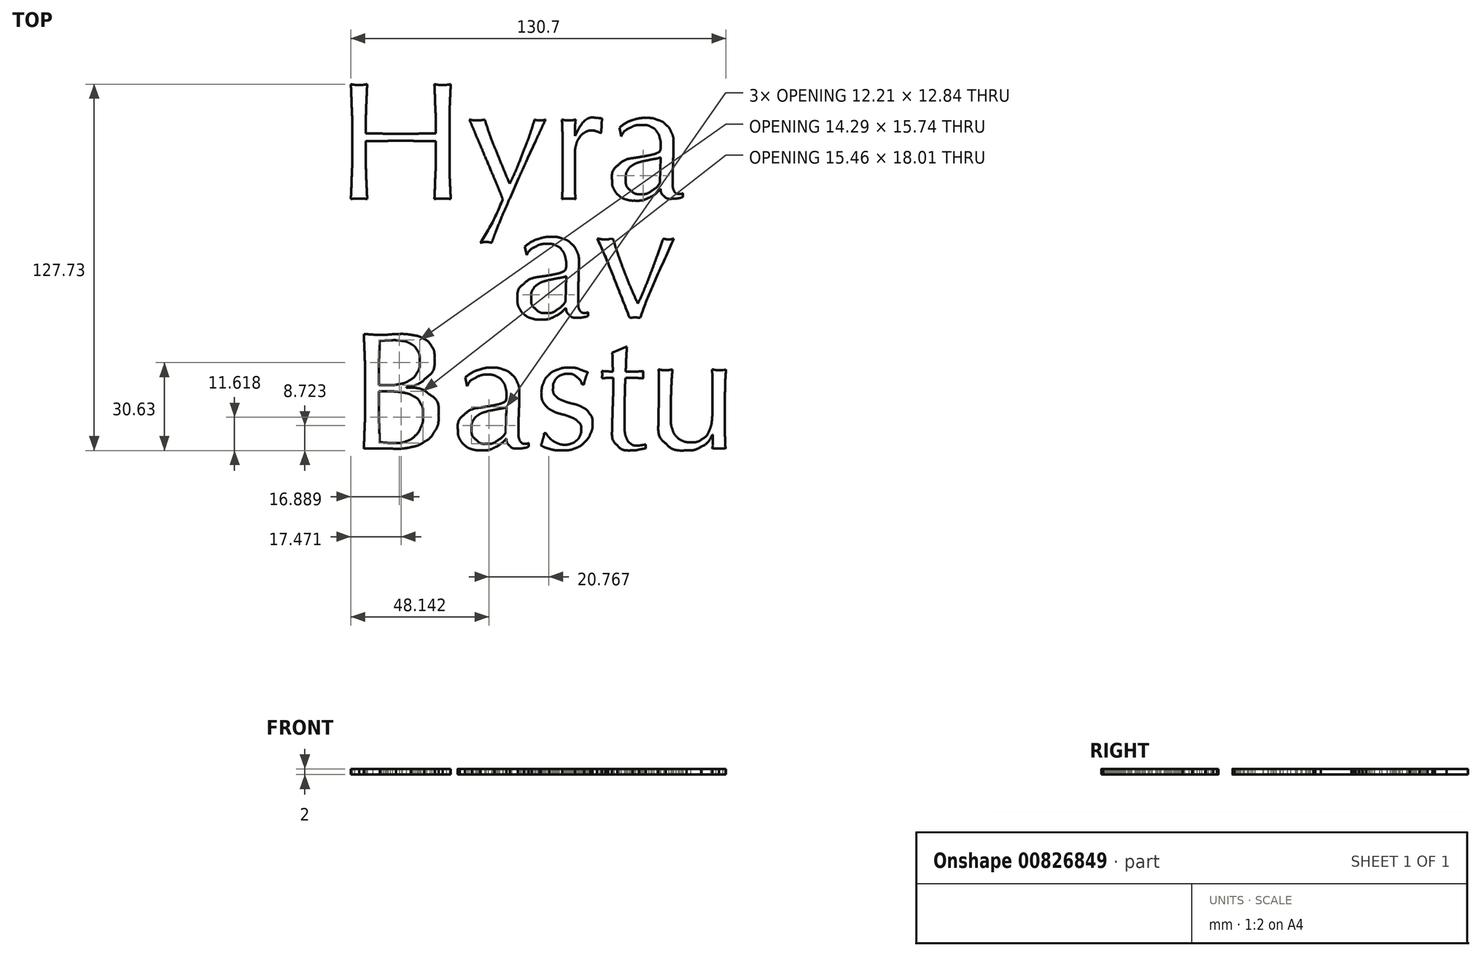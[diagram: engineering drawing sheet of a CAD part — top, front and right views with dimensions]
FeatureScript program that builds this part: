
annotation { "Feature Type Name" : "Feature", "Feature Type Description" : "" }
export const myFeature = defineFeature(function(context is Context, id is Id, definition is map)
    precondition{}
    {
        {
            var Q0;
            Q0=qCreatedBy(makeId("Top.planeOp"),FACE);
            var sketch = newSketch(context, id + "F0", { "sketchPlane" : qUnion([Q0])});
            skFitSpline(sketch, "E0", {"points": [v(-37.85, 47.17) * mm, v(-39.94, 47.13) * mm, v(-41.98, 47.09) * mm, v(-43.96, 47.05) * mm]});
            skFitSpline(sketch, "E1", {"points": [v(-43.96, 47.05) * mm, v(-45.9, 47.01) * mm, v(-47.92, 47) * mm, v(-50.01, 47) * mm]});
            skFitSpline(sketch, "E2", {"points": [v(-50.01, 47) * mm, v(-52.11, 47) * mm, v(-54.15, 47.01) * mm, v(-56.13, 47.05) * mm]});
            skFitSpline(sketch, "E3", {"points": [v(-56.13, 47.05) * mm, v(-58.07, 47.09) * mm, v(-60.09, 47.13) * mm, v(-62.18, 47.17) * mm]});
            skLineSegment(sketch, "E4", {"start": v(-37.85, 49.2) * mm, "end": v(-37.85, 47.17) * mm});
            skLineSegment(sketch, "E5", {"start": v(-37.85, 47.17) * mm, "end": v(-37.85, 49.2) * mm});
            skFitSpline(sketch, "E6", {"points": [v(-62.18, 49.2) * mm, v(-62.18, 51.77) * mm, v(-62.14, 54.27) * mm, v(-62.07, 56.72) * mm]});
            skFitSpline(sketch, "E7", {"points": [v(-62.07, 56.72) * mm, v(-61.95, 59.2) * mm, v(-61.83, 61.72) * mm, v(-61.72, 64.29) * mm]});
            skFitSpline(sketch, "E8", {"points": [v(-61.72, 64.29) * mm, v(-62.22, 64.2) * mm, v(-62.7, 64.13) * mm, v(-63.17, 64.05) * mm]});
            skFitSpline(sketch, "E9", {"points": [v(-63.17, 64.05) * mm, v(-63.64, 64.01) * mm, v(-64.1, 64) * mm, v(-64.57, 64) * mm]});
            skFitSpline(sketch, "E10", {"points": [v(-64.57, 64) * mm, v(-65.04, 64) * mm, v(-65.5, 64.01) * mm, v(-65.97, 64.05) * mm]});
            skFitSpline(sketch, "E11", {"points": [v(-65.97, 64.05) * mm, v(-66.43, 64.13) * mm, v(-66.92, 64.2) * mm, v(-67.42, 64.29) * mm]});
            skFitSpline(sketch, "E12", {"points": [v(-67.42, 64.29) * mm, v(-67.3, 61.72) * mm, v(-67.2, 59.2) * mm, v(-67.13, 56.72) * mm]});
            skFitSpline(sketch, "E13", {"points": [v(-67.13, 56.72) * mm, v(-67.02, 54.27) * mm, v(-66.96, 51.77) * mm, v(-66.96, 49.2) * mm]});
            skLineSegment(sketch, "E14", {"start": v(-62.18, 47.17) * mm, "end": v(-62.18, 49.2) * mm});
            skLineSegment(sketch, "E15", {"start": v(-62.18, 49.2) * mm, "end": v(-62.18, 47.17) * mm});
            skFitSpline(sketch, "E16", {"points": [v(-66.96, 39.2) * mm, v(-66.96, 36.63) * mm, v(-67.02, 34.1) * mm, v(-67.13, 31.62) * mm]});
            skFitSpline(sketch, "E17", {"points": [v(-67.13, 31.62) * mm, v(-67.2, 29.14) * mm, v(-67.3, 26.7) * mm, v(-67.42, 24.29) * mm]});
            skFitSpline(sketch, "E18", {"points": [v(-67.42, 24.29) * mm, v(-66.53, 24.36) * mm, v(-65.58, 24.4) * mm, v(-64.57, 24.4) * mm]});
            skFitSpline(sketch, "E19", {"points": [v(-64.57, 24.4) * mm, v(-63.56, 24.4) * mm, v(-62.61, 24.36) * mm, v(-61.72, 24.29) * mm]});
            skFitSpline(sketch, "E20", {"points": [v(-61.72, 24.29) * mm, v(-61.83, 26.7) * mm, v(-61.95, 29.14) * mm, v(-62.07, 31.62) * mm]});
            skFitSpline(sketch, "E21", {"points": [v(-62.07, 31.62) * mm, v(-62.14, 34.1) * mm, v(-62.18, 36.63) * mm, v(-62.18, 39.2) * mm]});
            skLineSegment(sketch, "E22", {"start": v(-66.96, 49.2) * mm, "end": v(-66.96, 39.2) * mm});
            skLineSegment(sketch, "E23", {"start": v(-66.96, 39.2) * mm, "end": v(-66.96, 49.2) * mm});
            skFitSpline(sketch, "E24", {"points": [v(-62.18, 44.43) * mm, v(-60.09, 44.47) * mm, v(-58.07, 44.49) * mm, v(-56.13, 44.49) * mm]});
            skFitSpline(sketch, "E25", {"points": [v(-56.13, 44.49) * mm, v(-54.15, 44.53) * mm, v(-52.11, 44.55) * mm, v(-50.01, 44.55) * mm]});
            skFitSpline(sketch, "E26", {"points": [v(-50.01, 44.55) * mm, v(-47.92, 44.55) * mm, v(-45.9, 44.53) * mm, v(-43.96, 44.49) * mm]});
            skFitSpline(sketch, "E27", {"points": [v(-43.96, 44.49) * mm, v(-41.98, 44.49) * mm, v(-39.94, 44.47) * mm, v(-37.85, 44.43) * mm]});
            skLineSegment(sketch, "E28", {"start": v(-62.18, 39.2) * mm, "end": v(-62.18, 44.43) * mm});
            skLineSegment(sketch, "E29", {"start": v(-62.18, 44.43) * mm, "end": v(-62.18, 39.2) * mm});
            skFitSpline(sketch, "E30", {"points": [v(-37.85, 39.2) * mm, v(-37.85, 36.63) * mm, v(-37.9, 34.1) * mm, v(-38.02, 31.62) * mm]});
            skFitSpline(sketch, "E31", {"points": [v(-38.02, 31.62) * mm, v(-38.1, 29.14) * mm, v(-38.2, 26.7) * mm, v(-38.31, 24.29) * mm]});
            skFitSpline(sketch, "E32", {"points": [v(-38.31, 24.29) * mm, v(-37.42, 24.36) * mm, v(-36.47, 24.4) * mm, v(-35.46, 24.4) * mm]});
            skFitSpline(sketch, "E33", {"points": [v(-35.46, 24.4) * mm, v(-34.45, 24.4) * mm, v(-33.5, 24.36) * mm, v(-32.6, 24.29) * mm]});
            skFitSpline(sketch, "E34", {"points": [v(-32.6, 24.29) * mm, v(-32.72, 26.7) * mm, v(-32.84, 29.14) * mm, v(-32.95, 31.62) * mm]});
            skFitSpline(sketch, "E35", {"points": [v(-32.95, 31.62) * mm, v(-33.03, 34.1) * mm, v(-33.07, 36.63) * mm, v(-33.07, 39.2) * mm]});
            skLineSegment(sketch, "E36", {"start": v(-37.85, 44.43) * mm, "end": v(-37.85, 39.2) * mm});
            skLineSegment(sketch, "E37", {"start": v(-37.85, 39.2) * mm, "end": v(-37.85, 44.43) * mm});
            skFitSpline(sketch, "E38", {"points": [v(-33.07, 49.2) * mm, v(-33.07, 51.77) * mm, v(-33.03, 54.27) * mm, v(-32.95, 56.72) * mm]});
            skFitSpline(sketch, "E39", {"points": [v(-32.95, 56.72) * mm, v(-32.84, 59.2) * mm, v(-32.72, 61.72) * mm, v(-32.6, 64.29) * mm]});
            skFitSpline(sketch, "E40", {"points": [v(-32.6, 64.29) * mm, v(-33.1, 64.2) * mm, v(-33.6, 64.13) * mm, v(-34.06, 64.05) * mm]});
            skFitSpline(sketch, "E41", {"points": [v(-34.06, 64.05) * mm, v(-34.53, 64.01) * mm, v(-35, 64) * mm, v(-35.46, 64) * mm]});
            skFitSpline(sketch, "E42", {"points": [v(-35.46, 64) * mm, v(-35.92, 64) * mm, v(-36.39, 64.01) * mm, v(-36.86, 64.05) * mm]});
            skFitSpline(sketch, "E43", {"points": [v(-36.86, 64.05) * mm, v(-37.32, 64.13) * mm, v(-37.8, 64.2) * mm, v(-38.31, 64.29) * mm]});
            skFitSpline(sketch, "E44", {"points": [v(-38.31, 64.29) * mm, v(-38.2, 61.72) * mm, v(-38.1, 59.2) * mm, v(-38.02, 56.72) * mm]});
            skFitSpline(sketch, "E45", {"points": [v(-38.02, 56.72) * mm, v(-37.9, 54.27) * mm, v(-37.85, 51.77) * mm, v(-37.85, 49.2) * mm]});
            skLineSegment(sketch, "E46", {"start": v(-33.07, 39.2) * mm, "end": v(-33.07, 49.2) * mm});
            skLineSegment(sketch, "E47", {"start": v(-33.07, 49.2) * mm, "end": v(-33.07, 39.2) * mm});
            skFitSpline(sketch, "E48", {"points": [v(-14.48, 24.23) * mm, v(-16.61, 19.14) * mm, v(-19.21, 14.06) * mm, v(-22.28, 8.97) * mm]});
            skFitSpline(sketch, "E49", {"points": [v(-22.28, 8.97) * mm, v(-21.5, 9.17) * mm, v(-20.84, 9.26) * mm, v(-20.3, 9.26) * mm]});
            skFitSpline(sketch, "E50", {"points": [v(-20.3, 9.26) * mm, v(-19.76, 9.26) * mm, v(-19.1, 9.17) * mm, v(-18.32, 8.97) * mm]});
            skFitSpline(sketch, "E51", {"points": [v(-18.32, 8.97) * mm, v(-18, 9.94) * mm, v(-17.54, 11.26) * mm, v(-16.92, 12.93) * mm]});
            skFitSpline(sketch, "E52", {"points": [v(-16.92, 12.93) * mm, v(-16.26, 14.56) * mm, v(-15.5, 16.4) * mm, v(-14.65, 18.46) * mm]});
            skFitSpline(sketch, "E53", {"points": [v(-14.65, 18.46) * mm, v(-13.8, 20.48) * mm, v(-12.87, 22.62) * mm, v(-11.86, 24.87) * mm]});
            skFitSpline(sketch, "E54", {"points": [v(-11.86, 24.87) * mm, v(-10.85, 27.16) * mm, v(-9.84, 29.45) * mm, v(-8.83, 31.74) * mm]});
            skFitSpline(sketch, "E55", {"points": [v(-8.83, 31.74) * mm, v(-7.78, 34.07) * mm, v(-6.77, 36.32) * mm, v(-5.8, 38.5) * mm]});
            skFitSpline(sketch, "E56", {"points": [v(-5.8, 38.5) * mm, v(-4.8, 40.7) * mm, v(-3.88, 42.7) * mm, v(-3.07, 44.49) * mm]});
            skFitSpline(sketch, "E57", {"points": [v(-3.07, 44.49) * mm, v(-2.21, 46.31) * mm, v(-1.5, 47.87) * mm, v(-0.91, 49.15) * mm]});
            skFitSpline(sketch, "E58", {"points": [v(-0.91, 49.15) * mm, v(-0.3, 50.47) * mm, v(0.16, 51.4) * mm, v(0.43, 51.94) * mm]});
            skFitSpline(sketch, "E59", {"points": [v(0.43, 51.94) * mm, v(-0.35, 51.75) * mm, v(-0.99, 51.65) * mm, v(-1.5, 51.65) * mm]});
            skFitSpline(sketch, "E60", {"points": [v(-1.5, 51.65) * mm, v(-2, 51.65) * mm, v(-2.64, 51.75) * mm, v(-3.42, 51.94) * mm]});
            skFitSpline(sketch, "E61", {"points": [v(-3.42, 51.94) * mm, v(-4.58, 48.22) * mm, v(-5.92, 44.41) * mm, v(-7.43, 40.53) * mm]});
            skFitSpline(sketch, "E62", {"points": [v(-7.43, 40.53) * mm, v(-8.9, 36.65) * mm, v(-10.46, 33) * mm, v(-12.1, 29.58) * mm]});
            skFitSpline(sketch, "E63", {"points": [v(-12.1, 29.58) * mm, v(-13.72, 33.47) * mm, v(-15.27, 37.23) * mm, v(-16.75, 40.88) * mm]});
            skFitSpline(sketch, "E64", {"points": [v(-16.75, 40.88) * mm, v(-18.22, 44.53) * mm, v(-19.56, 48.22) * mm, v(-20.77, 51.94) * mm]});
            skFitSpline(sketch, "E65", {"points": [v(-20.77, 51.94) * mm, v(-21.27, 51.86) * mm, v(-21.74, 51.79) * mm, v(-22.16, 51.7) * mm]});
            skFitSpline(sketch, "E66", {"points": [v(-22.16, 51.7) * mm, v(-22.6, 51.67) * mm, v(-23.02, 51.65) * mm, v(-23.44, 51.65) * mm]});
            skFitSpline(sketch, "E67", {"points": [v(-23.44, 51.65) * mm, v(-23.87, 51.65) * mm, v(-24.3, 51.67) * mm, v(-24.73, 51.7) * mm]});
            skFitSpline(sketch, "E68", {"points": [v(-24.73, 51.7) * mm, v(-25.15, 51.79) * mm, v(-25.62, 51.86) * mm, v(-26.12, 51.94) * mm]});
            skFitSpline(sketch, "E69", {"points": [v(-26.12, 51.94) * mm, v(-25.85, 51.32) * mm, v(-25.44, 50.37) * mm, v(-24.9, 49.09) * mm]});
            skFitSpline(sketch, "E70", {"points": [v(-24.9, 49.09) * mm, v(-24.36, 47.8) * mm, v(-23.74, 46.31) * mm, v(-23.04, 44.6) * mm]});
            skFitSpline(sketch, "E71", {"points": [v(-23.04, 44.6) * mm, v(-22.3, 42.94) * mm, v(-21.52, 41.13) * mm, v(-20.7, 39.2) * mm]});
            skFitSpline(sketch, "E72", {"points": [v(-20.7, 39.2) * mm, v(-19.9, 37.29) * mm, v(-19.1, 35.4) * mm, v(-18.32, 33.54) * mm]});
            skFitSpline(sketch, "E73", {"points": [v(-18.32, 33.54) * mm, v(-17.54, 31.72) * mm, v(-16.83, 29.97) * mm, v(-16.17, 28.3) * mm]});
            skFitSpline(sketch, "E74", {"points": [v(-16.17, 28.3) * mm, v(-15.47, 26.63) * mm, v(-14.9, 25.28) * mm, v(-14.48, 24.23) * mm]});
            skFitSpline(sketch, "E75", {"points": [v(19.87, 47.46) * mm, v(19.87, 48.23) * mm, v(19.9, 49.09) * mm, v(19.93, 50.02) * mm]});
            skFitSpline(sketch, "E76", {"points": [v(19.93, 50.02) * mm, v(19.97, 51) * mm, v(20.09, 51.7) * mm, v(20.28, 52.17) * mm]});
            skFitSpline(sketch, "E77", {"points": [v(20.28, 52.17) * mm, v(19.9, 52.33) * mm, v(19.56, 52.43) * mm, v(19.3, 52.47) * mm]});
            skFitSpline(sketch, "E78", {"points": [v(19.3, 52.47) * mm, v(19.06, 52.5) * mm, v(18.77, 52.52) * mm, v(18.42, 52.52) * mm]});
            skFitSpline(sketch, "E79", {"points": [v(18.42, 52.52) * mm, v(15.59, 52.52) * mm, v(13.02, 50.43) * mm, v(10.73, 46.24) * mm]});
            skLineSegment(sketch, "E80", {"start": v(19.47, 47.17) * mm, "end": v(19.87, 47.46) * mm});
            skLineSegment(sketch, "E81", {"start": v(19.87, 47.46) * mm, "end": v(19.47, 47.17) * mm});
            skFitSpline(sketch, "E82", {"points": [v(10.62, 46.3) * mm, v(10.62, 47.03) * mm, v(10.62, 47.8) * mm, v(10.62, 48.62) * mm]});
            skFitSpline(sketch, "E83", {"points": [v(10.62, 48.62) * mm, v(10.66, 49.44) * mm, v(10.75, 50.54) * mm, v(10.9, 51.94) * mm]});
            skFitSpline(sketch, "E84", {"points": [v(10.9, 51.94) * mm, v(10.48, 51.86) * mm, v(10.07, 51.79) * mm, v(9.69, 51.7) * mm]});
            skFitSpline(sketch, "E85", {"points": [v(9.69, 51.7) * mm, v(9.3, 51.67) * mm, v(8.93, 51.65) * mm, v(8.58, 51.65) * mm]});
            skFitSpline(sketch, "E86", {"points": [v(8.58, 51.65) * mm, v(8.15, 51.65) * mm, v(7.74, 51.67) * mm, v(7.36, 51.7) * mm]});
            skFitSpline(sketch, "E87", {"points": [v(7.36, 51.7) * mm, v(6.97, 51.79) * mm, v(6.56, 51.86) * mm, v(6.13, 51.94) * mm]});
            skFitSpline(sketch, "E88", {"points": [v(6.13, 51.94) * mm, v(6.25, 49.38) * mm, v(6.3, 47.1) * mm, v(6.3, 45.13) * mm]});
            skFitSpline(sketch, "E89", {"points": [v(6.3, 45.13) * mm, v(6.35, 43.15) * mm, v(6.37, 41.4) * mm, v(6.37, 39.89) * mm]});
            skLineSegment(sketch, "E90", {"start": v(10.73, 46.24) * mm, "end": v(10.62, 46.3) * mm});
            skLineSegment(sketch, "E91", {"start": v(10.62, 46.3) * mm, "end": v(10.73, 46.24) * mm});
            skFitSpline(sketch, "E92", {"points": [v(6.37, 38.03) * mm, v(6.37, 34.73) * mm, v(6.35, 31.93) * mm, v(6.3, 29.64) * mm]});
            skFitSpline(sketch, "E93", {"points": [v(6.3, 29.64) * mm, v(6.3, 27.4) * mm, v(6.25, 25.6) * mm, v(6.13, 24.29) * mm]});
            skFitSpline(sketch, "E94", {"points": [v(6.13, 24.29) * mm, v(6.91, 24.36) * mm, v(7.73, 24.4) * mm, v(8.58, 24.4) * mm]});
            skFitSpline(sketch, "E95", {"points": [v(8.58, 24.4) * mm, v(9.36, 24.4) * mm, v(10.13, 24.36) * mm, v(10.9, 24.29) * mm]});
            skFitSpline(sketch, "E96", {"points": [v(10.9, 24.29) * mm, v(10.8, 25.14) * mm, v(10.71, 26.25) * mm, v(10.68, 27.6) * mm]});
            skFitSpline(sketch, "E97", {"points": [v(10.68, 27.6) * mm, v(10.68, 29) * mm, v(10.68, 31) * mm, v(10.68, 33.6) * mm]});
            skLineSegment(sketch, "E98", {"start": v(6.37, 39.89) * mm, "end": v(6.37, 38.03) * mm});
            skLineSegment(sketch, "E99", {"start": v(6.37, 38.03) * mm, "end": v(6.37, 39.89) * mm});
            skFitSpline(sketch, "E100", {"points": [v(10.68, 40) * mm, v(10.68, 41.13) * mm, v(10.81, 42.18) * mm, v(11.08, 43.15) * mm]});
            skFitSpline(sketch, "E101", {"points": [v(11.08, 43.15) * mm, v(11.35, 44.16) * mm, v(11.74, 45.01) * mm, v(12.25, 45.71) * mm]});
            skFitSpline(sketch, "E102", {"points": [v(12.25, 45.71) * mm, v(12.75, 46.45) * mm, v(13.37, 47.03) * mm, v(14.11, 47.46) * mm]});
            skFitSpline(sketch, "E103", {"points": [v(14.11, 47.46) * mm, v(14.85, 47.89) * mm, v(15.68, 48.1) * mm, v(16.61, 48.1) * mm]});
            skFitSpline(sketch, "E104", {"points": [v(16.61, 48.1) * mm, v(17.2, 48.1) * mm, v(17.76, 48) * mm, v(18.3, 47.8) * mm]});
            skFitSpline(sketch, "E105", {"points": [v(18.3, 47.8) * mm, v(18.88, 47.61) * mm, v(19.27, 47.4) * mm, v(19.47, 47.17) * mm]});
            skLineSegment(sketch, "E106", {"start": v(10.68, 33.6) * mm, "end": v(10.68, 40) * mm});
            skLineSegment(sketch, "E107", {"start": v(10.68, 40) * mm, "end": v(10.68, 33.6) * mm});
            skFitSpline(sketch, "E108", {"points": [v(40.31, 30.05) * mm, v(39.65, 28.96) * mm, v(38.7, 28.01) * mm, v(37.46, 27.2) * mm]});
            skFitSpline(sketch, "E109", {"points": [v(37.46, 27.2) * mm, v(36.25, 26.38) * mm, v(34.91, 25.97) * mm, v(33.44, 25.97) * mm]});
            skFitSpline(sketch, "E110", {"points": [v(33.44, 25.97) * mm, v(32.16, 25.97) * mm, v(31, 26.44) * mm, v(29.95, 27.37) * mm]});
            skFitSpline(sketch, "E111", {"points": [v(29.95, 27.37) * mm, v(28.9, 28.3) * mm, v(28.37, 29.68) * mm, v(28.37, 31.5) * mm]});
            skFitSpline(sketch, "E112", {"points": [v(28.37, 31.5) * mm, v(28.37, 32.6) * mm, v(28.57, 33.48) * mm, v(28.96, 34.18) * mm]});
            skFitSpline(sketch, "E113", {"points": [v(28.96, 34.18) * mm, v(29.38, 34.88) * mm, v(29.93, 35.46) * mm, v(30.59, 35.93) * mm]});
            skFitSpline(sketch, "E114", {"points": [v(30.59, 35.93) * mm, v(31.29, 36.4) * mm, v(32.06, 36.76) * mm, v(32.92, 37.04) * mm]});
            skFitSpline(sketch, "E115", {"points": [v(32.92, 37.04) * mm, v(33.8, 37.3) * mm, v(34.7, 37.52) * mm, v(35.6, 37.68) * mm]});
            skFitSpline(sketch, "E116", {"points": [v(35.6, 37.68) * mm, v(36.49, 37.87) * mm, v(37.36, 38.05) * mm, v(38.21, 38.2) * mm]});
            skFitSpline(sketch, "E117", {"points": [v(38.21, 38.2) * mm, v(39.1, 38.36) * mm, v(39.88, 38.55) * mm, v(40.54, 38.78) * mm]});
            skLineSegment(sketch, "E118", {"start": v(40.54, 38.78) * mm, "end": v(40.31, 30.05) * mm});
            skLineSegment(sketch, "E119", {"start": v(40.31, 30.05) * mm, "end": v(40.54, 38.78) * mm});
            skFitSpline(sketch, "E120", {"points": [v(26.8, 46.12) * mm, v(27.46, 47.36) * mm, v(28.45, 48.33) * mm, v(29.77, 49.03) * mm]});
            skFitSpline(sketch, "E121", {"points": [v(29.77, 49.03) * mm, v(31.13, 49.73) * mm, v(32.59, 50.08) * mm, v(34.14, 50.08) * mm]});
            skFitSpline(sketch, "E122", {"points": [v(34.14, 50.08) * mm, v(35.3, 50.08) * mm, v(36.3, 49.87) * mm, v(37.1, 49.44) * mm]});
            skFitSpline(sketch, "E123", {"points": [v(37.1, 49.44) * mm, v(37.92, 49.05) * mm, v(38.58, 48.53) * mm, v(39.09, 47.87) * mm]});
            skFitSpline(sketch, "E124", {"points": [v(39.09, 47.87) * mm, v(39.6, 47.2) * mm, v(39.96, 46.43) * mm, v(40.2, 45.54) * mm]});
            skFitSpline(sketch, "E125", {"points": [v(40.2, 45.54) * mm, v(40.43, 44.64) * mm, v(40.54, 43.71) * mm, v(40.54, 42.74) * mm]});
            skFitSpline(sketch, "E126", {"points": [v(40.54, 42.74) * mm, v(40.54, 42.16) * mm, v(40.49, 41.67) * mm, v(40.37, 41.29) * mm]});
            skFitSpline(sketch, "E127", {"points": [v(40.37, 41.29) * mm, v(40.25, 40.94) * mm, v(39.9, 40.63) * mm, v(39.32, 40.36) * mm]});
            skFitSpline(sketch, "E128", {"points": [v(39.32, 40.36) * mm, v(38.78, 40.08) * mm, v(37.9, 39.81) * mm, v(36.7, 39.54) * mm]});
            skFitSpline(sketch, "E129", {"points": [v(36.7, 39.54) * mm, v(35.54, 39.3) * mm, v(33.9, 39.02) * mm, v(31.8, 38.67) * mm]});
            skFitSpline(sketch, "E130", {"points": [v(31.8, 38.67) * mm, v(29.25, 38.24) * mm, v(27.23, 37.39) * mm, v(25.75, 36.1) * mm]});
            skFitSpline(sketch, "E131", {"points": [v(25.75, 36.1) * mm, v(24.32, 34.82) * mm, v(23.6, 33.02) * mm, v(23.6, 30.69) * mm]});
            skFitSpline(sketch, "E132", {"points": [v(23.6, 30.69) * mm, v(23.6, 29.56) * mm, v(23.81, 28.56) * mm, v(24.24, 27.66) * mm]});
            skFitSpline(sketch, "E133", {"points": [v(24.24, 27.66) * mm, v(24.7, 26.8) * mm, v(25.29, 26.07) * mm, v(25.99, 25.45) * mm]});
            skFitSpline(sketch, "E134", {"points": [v(25.99, 25.45) * mm, v(26.72, 24.83) * mm, v(27.56, 24.38) * mm, v(28.5, 24.11) * mm]});
            skFitSpline(sketch, "E135", {"points": [v(28.5, 24.11) * mm, v(29.42, 23.84) * mm, v(30.37, 23.7) * mm, v(31.34, 23.7) * mm]});
            skFitSpline(sketch, "E136", {"points": [v(31.34, 23.7) * mm, v(33.32, 23.7) * mm, v(35, 24.03) * mm, v(36.35, 24.7) * mm]});
            skFitSpline(sketch, "E137", {"points": [v(36.35, 24.7) * mm, v(37.7, 25.35) * mm, v(39.09, 26.38) * mm, v(40.49, 27.78) * mm]});
            skFitSpline(sketch, "E138", {"points": [v(40.49, 27.78) * mm, v(40.6, 26.77) * mm, v(40.99, 25.93) * mm, v(41.65, 25.28) * mm]});
            skFitSpline(sketch, "E139", {"points": [v(41.65, 25.28) * mm, v(42.3, 24.65) * mm, v(43.26, 24.34) * mm, v(44.5, 24.34) * mm]});
            skFitSpline(sketch, "E140", {"points": [v(44.5, 24.34) * mm, v(45.28, 24.34) * mm, v(45.98, 24.4) * mm, v(46.6, 24.52) * mm]});
            skFitSpline(sketch, "E141", {"points": [v(46.6, 24.52) * mm, v(47.26, 24.63) * mm, v(47.8, 24.79) * mm, v(48.23, 24.98) * mm]});
            skLineSegment(sketch, "E142", {"start": v(26.16, 49.15) * mm, "end": v(26.16, 46.12) * mm});
            skLineSegment(sketch, "E143", {"start": v(26.16, 46.12) * mm, "end": v(26.8, 46.12) * mm});
            skLineSegment(sketch, "E144", {"start": v(26.8, 46.12) * mm, "end": v(26.16, 49.15) * mm});
            skFitSpline(sketch, "E145", {"points": [v(48.23, 26.26) * mm, v(48.03, 26.15) * mm, v(47.82, 26.07) * mm, v(47.59, 26.03) * mm]});
            skFitSpline(sketch, "E146", {"points": [v(47.59, 26.03) * mm, v(47.4, 26.03) * mm, v(47.2, 26.03) * mm, v(47, 26.03) * mm]});
            skFitSpline(sketch, "E147", {"points": [v(47, 26.03) * mm, v(46.42, 26.03) * mm, v(45.98, 26.17) * mm, v(45.67, 26.44) * mm]});
            skFitSpline(sketch, "E148", {"points": [v(45.67, 26.44) * mm, v(45.4, 26.71) * mm, v(45.18, 27.04) * mm, v(45.03, 27.43) * mm]});
            skFitSpline(sketch, "E149", {"points": [v(45.03, 27.43) * mm, v(44.87, 27.86) * mm, v(44.77, 28.32) * mm, v(44.74, 28.83) * mm]});
            skFitSpline(sketch, "E150", {"points": [v(44.74, 28.83) * mm, v(44.74, 29.37) * mm, v(44.74, 29.87) * mm, v(44.74, 30.34) * mm]});
            skFitSpline(sketch, "E151", {"points": [v(44.74, 30.34) * mm, v(44.74, 32.79) * mm, v(44.77, 35.1) * mm, v(44.85, 37.27) * mm]});
            skFitSpline(sketch, "E152", {"points": [v(44.85, 37.27) * mm, v(44.93, 39.48) * mm, v(44.97, 41.7) * mm, v(44.97, 43.9) * mm]});
            skFitSpline(sketch, "E153", {"points": [v(44.97, 43.9) * mm, v(44.97, 45.19) * mm, v(44.74, 46.35) * mm, v(44.27, 47.4) * mm]});
            skFitSpline(sketch, "E154", {"points": [v(44.27, 47.4) * mm, v(43.8, 48.49) * mm, v(43.16, 49.4) * mm, v(42.35, 50.14) * mm]});
            skFitSpline(sketch, "E155", {"points": [v(42.35, 50.14) * mm, v(41.53, 50.91) * mm, v(40.54, 51.5) * mm, v(39.38, 51.88) * mm]});
            skFitSpline(sketch, "E156", {"points": [v(39.38, 51.88) * mm, v(38.21, 52.31) * mm, v(36.93, 52.52) * mm, v(35.54, 52.52) * mm]});
            skFitSpline(sketch, "E157", {"points": [v(35.54, 52.52) * mm, v(33.98, 52.52) * mm, v(32.47, 52.3) * mm, v(31, 51.83) * mm]});
            skFitSpline(sketch, "E158", {"points": [v(31, 51.83) * mm, v(29.52, 51.36) * mm, v(27.9, 50.47) * mm, v(26.16, 49.15) * mm]});
            skLineSegment(sketch, "E159", {"start": v(48.23, 24.98) * mm, "end": v(48.23, 26.26) * mm});
            skLineSegment(sketch, "E160", {"start": v(48.23, 26.26) * mm, "end": v(48.23, 24.98) * mm});
            skFitSpline(sketch, "E161", {"points": [v(7.36, -11.42) * mm, v(6.7, -12.5) * mm, v(5.75, -13.45) * mm, v(4.5, -14.27) * mm]});
            skFitSpline(sketch, "E162", {"points": [v(4.5, -14.27) * mm, v(3.3, -15.09) * mm, v(1.97, -15.5) * mm, v(0.5, -15.5) * mm]});
            skFitSpline(sketch, "E163", {"points": [v(0.5, -15.5) * mm, v(-0.79, -15.5) * mm, v(-1.95, -15.03) * mm, v(-3, -14.1) * mm]});
            skFitSpline(sketch, "E164", {"points": [v(-3, -14.1) * mm, v(-4.05, -13.16) * mm, v(-4.57, -11.79) * mm, v(-4.57, -9.96) * mm]});
            skFitSpline(sketch, "E165", {"points": [v(-4.57, -9.96) * mm, v(-4.57, -8.87) * mm, v(-4.38, -7.98) * mm, v(-4, -7.28) * mm]});
            skFitSpline(sketch, "E166", {"points": [v(-4, -7.28) * mm, v(-3.57, -6.58) * mm, v(-3.02, -6) * mm, v(-2.36, -5.54) * mm]});
            skFitSpline(sketch, "E167", {"points": [v(-2.36, -5.54) * mm, v(-1.66, -5.07) * mm, v(-0.89, -4.7) * mm, v(-0.03, -4.43) * mm]});
            skFitSpline(sketch, "E168", {"points": [v(-0.03, -4.43) * mm, v(0.86, -4.16) * mm, v(1.75, -3.94) * mm, v(2.65, -3.79) * mm]});
            skFitSpline(sketch, "E169", {"points": [v(2.65, -3.79) * mm, v(3.54, -3.6) * mm, v(4.41, -3.42) * mm, v(5.27, -3.27) * mm]});
            skFitSpline(sketch, "E170", {"points": [v(5.27, -3.27) * mm, v(6.16, -3.11) * mm, v(6.93, -2.92) * mm, v(7.6, -2.68) * mm]});
            skLineSegment(sketch, "E171", {"start": v(7.6, -2.68) * mm, "end": v(7.36, -11.42) * mm});
            skLineSegment(sketch, "E172", {"start": v(7.36, -11.42) * mm, "end": v(7.6, -2.68) * mm});
            skFitSpline(sketch, "E173", {"points": [v(-6.15, 4.65) * mm, v(-5.49, 5.9) * mm, v(-4.5, 6.87) * mm, v(-3.18, 7.56) * mm]});
            skFitSpline(sketch, "E174", {"points": [v(-3.18, 7.56) * mm, v(-1.82, 8.26) * mm, v(-0.36, 8.61) * mm, v(1.19, 8.61) * mm]});
            skFitSpline(sketch, "E175", {"points": [v(1.19, 8.61) * mm, v(2.35, 8.61) * mm, v(3.34, 8.4) * mm, v(4.16, 7.97) * mm]});
            skFitSpline(sketch, "E176", {"points": [v(4.16, 7.97) * mm, v(4.97, 7.58) * mm, v(5.63, 7.06) * mm, v(6.14, 6.4) * mm]});
            skFitSpline(sketch, "E177", {"points": [v(6.14, 6.4) * mm, v(6.64, 5.74) * mm, v(7.01, 4.96) * mm, v(7.25, 4.07) * mm]});
            skFitSpline(sketch, "E178", {"points": [v(7.25, 4.07) * mm, v(7.48, 3.18) * mm, v(7.6, 2.25) * mm, v(7.6, 1.28) * mm]});
            skFitSpline(sketch, "E179", {"points": [v(7.6, 1.28) * mm, v(7.6, 0.7) * mm, v(7.54, 0.2) * mm, v(7.42, -0.18) * mm]});
            skFitSpline(sketch, "E180", {"points": [v(7.42, -0.18) * mm, v(7.3, -0.53) * mm, v(6.95, -0.84) * mm, v(6.37, -1.11) * mm]});
            skFitSpline(sketch, "E181", {"points": [v(6.37, -1.11) * mm, v(5.83, -1.38) * mm, v(4.95, -1.65) * mm, v(3.75, -1.93) * mm]});
            skFitSpline(sketch, "E182", {"points": [v(3.75, -1.93) * mm, v(2.59, -2.16) * mm, v(0.96, -2.45) * mm, v(-1.14, -2.8) * mm]});
            skFitSpline(sketch, "E183", {"points": [v(-1.14, -2.8) * mm, v(-3.7, -3.23) * mm, v(-5.72, -4.08) * mm, v(-7.2, -5.36) * mm]});
            skFitSpline(sketch, "E184", {"points": [v(-7.2, -5.36) * mm, v(-8.63, -6.64) * mm, v(-9.35, -8.45) * mm, v(-9.35, -10.78) * mm]});
            skFitSpline(sketch, "E185", {"points": [v(-9.35, -10.78) * mm, v(-9.35, -11.9) * mm, v(-9.14, -12.91) * mm, v(-8.7, -13.8) * mm]});
            skFitSpline(sketch, "E186", {"points": [v(-8.7, -13.8) * mm, v(-8.24, -14.66) * mm, v(-7.66, -15.4) * mm, v(-6.96, -16.02) * mm]});
            skFitSpline(sketch, "E187", {"points": [v(-6.96, -16.02) * mm, v(-6.22, -16.64) * mm, v(-5.39, -17.08) * mm, v(-4.46, -17.36) * mm]});
            skFitSpline(sketch, "E188", {"points": [v(-4.46, -17.36) * mm, v(-3.53, -17.63) * mm, v(-2.58, -17.76) * mm, v(-1.6, -17.76) * mm]});
            skFitSpline(sketch, "E189", {"points": [v(-1.6, -17.76) * mm, v(0.37, -17.76) * mm, v(2.04, -17.43) * mm, v(3.4, -16.77) * mm]});
            skFitSpline(sketch, "E190", {"points": [v(3.4, -16.77) * mm, v(4.76, -16.11) * mm, v(6.14, -15.09) * mm, v(7.54, -13.69) * mm]});
            skFitSpline(sketch, "E191", {"points": [v(7.54, -13.69) * mm, v(7.65, -14.7) * mm, v(8.04, -15.53) * mm, v(8.7, -16.2) * mm]});
            skFitSpline(sketch, "E192", {"points": [v(8.7, -16.2) * mm, v(9.36, -16.81) * mm, v(10.31, -17.12) * mm, v(11.55, -17.12) * mm]});
            skFitSpline(sketch, "E193", {"points": [v(11.55, -17.12) * mm, v(12.33, -17.12) * mm, v(13.03, -17.06) * mm, v(13.65, -16.95) * mm]});
            skFitSpline(sketch, "E194", {"points": [v(13.65, -16.95) * mm, v(14.3, -16.83) * mm, v(14.85, -16.68) * mm, v(15.28, -16.48) * mm]});
            skLineSegment(sketch, "E195", {"start": v(-6.79, 7.68) * mm, "end": v(-6.79, 4.65) * mm});
            skLineSegment(sketch, "E196", {"start": v(-6.79, 4.65) * mm, "end": v(-6.15, 4.65) * mm});
            skLineSegment(sketch, "E197", {"start": v(-6.15, 4.65) * mm, "end": v(-6.79, 7.68) * mm});
            skFitSpline(sketch, "E198", {"points": [v(15.28, -15.2) * mm, v(15.09, -15.32) * mm, v(14.87, -15.4) * mm, v(14.64, -15.43) * mm]});
            skFitSpline(sketch, "E199", {"points": [v(14.64, -15.43) * mm, v(14.45, -15.43) * mm, v(14.25, -15.43) * mm, v(14.06, -15.43) * mm]});
            skFitSpline(sketch, "E200", {"points": [v(14.06, -15.43) * mm, v(13.48, -15.43) * mm, v(13.03, -15.3) * mm, v(12.72, -15.03) * mm]});
            skFitSpline(sketch, "E201", {"points": [v(12.72, -15.03) * mm, v(12.45, -14.76) * mm, v(12.23, -14.43) * mm, v(12.08, -14.04) * mm]});
            skFitSpline(sketch, "E202", {"points": [v(12.08, -14.04) * mm, v(11.92, -13.61) * mm, v(11.83, -13.14) * mm, v(11.79, -12.64) * mm]});
            skFitSpline(sketch, "E203", {"points": [v(11.79, -12.64) * mm, v(11.79, -12.1) * mm, v(11.79, -11.6) * mm, v(11.79, -11.13) * mm]});
            skFitSpline(sketch, "E204", {"points": [v(11.79, -11.13) * mm, v(11.79, -8.68) * mm, v(11.83, -6.37) * mm, v(11.9, -4.2) * mm]});
            skFitSpline(sketch, "E205", {"points": [v(11.9, -4.2) * mm, v(11.98, -1.98) * mm, v(12.02, 0.23) * mm, v(12.02, 2.44) * mm]});
            skFitSpline(sketch, "E206", {"points": [v(12.02, 2.44) * mm, v(12.02, 3.72) * mm, v(11.79, 4.89) * mm, v(11.32, 5.93) * mm]});
            skFitSpline(sketch, "E207", {"points": [v(11.32, 5.93) * mm, v(10.86, 7.02) * mm, v(10.21, 7.93) * mm, v(9.4, 8.67) * mm]});
            skFitSpline(sketch, "E208", {"points": [v(9.4, 8.67) * mm, v(8.58, 9.45) * mm, v(7.6, 10.03) * mm, v(6.43, 10.42) * mm]});
            skFitSpline(sketch, "E209", {"points": [v(6.43, 10.42) * mm, v(5.27, 10.84) * mm, v(3.98, 11.06) * mm, v(2.59, 11.06) * mm]});
            skFitSpline(sketch, "E210", {"points": [v(2.59, 11.06) * mm, v(1.03, 11.06) * mm, v(-0.48, 10.82) * mm, v(-1.95, 10.36) * mm]});
            skFitSpline(sketch, "E211", {"points": [v(-1.95, 10.36) * mm, v(-3.43, 9.9) * mm, v(-5.04, 9) * mm, v(-6.79, 7.68) * mm]});
            skLineSegment(sketch, "E212", {"start": v(15.28, -16.48) * mm, "end": v(15.28, -15.2) * mm});
            skLineSegment(sketch, "E213", {"start": v(15.28, -15.2) * mm, "end": v(15.28, -16.48) * mm});
            skFitSpline(sketch, "E214", {"points": [v(29.72, -17.18) * mm, v(30.34, -17.1) * mm, v(30.96, -17.06) * mm, v(31.59, -17.06) * mm]});
            skFitSpline(sketch, "E215", {"points": [v(31.59, -17.06) * mm, v(32.2, -17.06) * mm, v(32.8, -17.1) * mm, v(33.4, -17.18) * mm]});
            skFitSpline(sketch, "E216", {"points": [v(33.4, -17.18) * mm, v(35.06, -12.6) * mm, v(36.9, -8.02) * mm, v(38.92, -3.44) * mm]});
            skFitSpline(sketch, "E217", {"points": [v(38.92, -3.44) * mm, v(40.94, 1.14) * mm, v(43, 5.78) * mm, v(45.1, 10.48) * mm]});
            skFitSpline(sketch, "E218", {"points": [v(45.1, 10.48) * mm, v(44.4, 10.28) * mm, v(43.8, 10.18) * mm, v(43.29, 10.18) * mm]});
            skFitSpline(sketch, "E219", {"points": [v(43.29, 10.18) * mm, v(42.78, 10.18) * mm, v(42.18, 10.28) * mm, v(41.48, 10.48) * mm]});
            skFitSpline(sketch, "E220", {"points": [v(41.48, 10.48) * mm, v(40.78, 8.57) * mm, v(40.07, 6.61) * mm, v(39.33, 4.6) * mm]});
            skFitSpline(sketch, "E221", {"points": [v(39.33, 4.6) * mm, v(38.63, 2.61) * mm, v(37.9, 0.64) * mm, v(37.12, -1.34) * mm]});
            skFitSpline(sketch, "E222", {"points": [v(37.12, -1.34) * mm, v(36.38, -3.32) * mm, v(35.62, -5.25) * mm, v(34.85, -7.1) * mm]});
            skFitSpline(sketch, "E223", {"points": [v(34.85, -7.1) * mm, v(34.1, -8.93) * mm, v(33.35, -10.64) * mm, v(32.58, -12.23) * mm]});
            skFitSpline(sketch, "E224", {"points": [v(32.58, -12.23) * mm, v(30.83, -8.35) * mm, v(29.24, -4.57) * mm, v(27.8, -0.88) * mm]});
            skFitSpline(sketch, "E225", {"points": [v(27.8, -0.88) * mm, v(26.4, 2.85) * mm, v(25.1, 6.63) * mm, v(23.9, 10.48) * mm]});
            skFitSpline(sketch, "E226", {"points": [v(23.9, 10.48) * mm, v(23.47, 10.4) * mm, v(23.05, 10.32) * mm, v(22.62, 10.24) * mm]});
            skFitSpline(sketch, "E227", {"points": [v(22.62, 10.24) * mm, v(22.2, 10.2) * mm, v(21.77, 10.18) * mm, v(21.34, 10.18) * mm]});
            skFitSpline(sketch, "E228", {"points": [v(21.34, 10.18) * mm, v(20.83, 10.18) * mm, v(20.35, 10.2) * mm, v(19.88, 10.24) * mm]});
            skFitSpline(sketch, "E229", {"points": [v(19.88, 10.24) * mm, v(19.42, 10.32) * mm, v(18.93, 10.4) * mm, v(18.43, 10.48) * mm]});
            skFitSpline(sketch, "E230", {"points": [v(18.43, 10.48) * mm, v(20.56, 5.78) * mm, v(22.52, 1.14) * mm, v(24.3, -3.44) * mm]});
            skFitSpline(sketch, "E231", {"points": [v(24.3, -3.44) * mm, v(26.13, -8.02) * mm, v(27.94, -12.6) * mm, v(29.72, -17.18) * mm]});
            skFitSpline(sketch, "E232", {"points": [v(-55.05, -42.82) * mm, v(-53.11, -42.82) * mm, v(-51.37, -42.94) * mm, v(-49.81, -43.17) * mm]});
            skFitSpline(sketch, "E233", {"points": [v(-49.81, -43.17) * mm, v(-48.22, -43.4) * mm, v(-46.86, -43.83) * mm, v(-45.74, -44.45) * mm]});
            skFitSpline(sketch, "E234", {"points": [v(-45.74, -44.45) * mm, v(-44.61, -45.04) * mm, v(-43.76, -45.87) * mm, v(-43.18, -46.96) * mm]});
            skFitSpline(sketch, "E235", {"points": [v(-43.18, -46.96) * mm, v(-42.56, -48) * mm, v(-42.25, -49.36) * mm, v(-42.25, -51.03) * mm]});
            skFitSpline(sketch, "E236", {"points": [v(-42.25, -51.03) * mm, v(-42.25, -52.59) * mm, v(-42.5, -53.98) * mm, v(-43, -55.23) * mm]});
            skFitSpline(sketch, "E237", {"points": [v(-43, -55.23) * mm, v(-43.5, -56.43) * mm, v(-44.19, -57.46) * mm, v(-45.04, -58.31) * mm]});
            skFitSpline(sketch, "E238", {"points": [v(-45.04, -58.31) * mm, v(-45.9, -59.13) * mm, v(-46.9, -59.75) * mm, v(-48.07, -60.17) * mm]});
            skFitSpline(sketch, "E239", {"points": [v(-48.07, -60.17) * mm, v(-49.2, -60.6) * mm, v(-50.38, -60.81) * mm, v(-51.62, -60.81) * mm]});
            skFitSpline(sketch, "E240", {"points": [v(-51.62, -60.81) * mm, v(-52.67, -60.81) * mm, v(-53.7, -60.8) * mm, v(-54.7, -60.76) * mm]});
            skFitSpline(sketch, "E241", {"points": [v(-54.7, -60.76) * mm, v(-55.71, -60.68) * mm, v(-56.59, -60.6) * mm, v(-57.33, -60.52) * mm]});
            skFitSpline(sketch, "E242", {"points": [v(-57.33, -60.52) * mm, v(-57.4, -58.54) * mm, v(-57.48, -56.58) * mm, v(-57.56, -54.64) * mm]});
            skFitSpline(sketch, "E243", {"points": [v(-57.56, -54.64) * mm, v(-57.64, -52.7) * mm, v(-57.67, -50.74) * mm, v(-57.67, -48.76) * mm]});
            skLineSegment(sketch, "E244", {"start": v(-57.67, -48.76) * mm, "end": v(-57.67, -42.82) * mm});
            skLineSegment(sketch, "E245", {"start": v(-57.67, -42.82) * mm, "end": v(-55.05, -42.82) * mm});
            skLineSegment(sketch, "E246", {"start": v(-55.05, -42.82) * mm, "end": v(-57.67, -48.76) * mm});
            skFitSpline(sketch, "E247", {"points": [v(-57.67, -36.3) * mm, v(-57.67, -34.44) * mm, v(-57.64, -32.6) * mm, v(-57.56, -30.77) * mm]});
            skFitSpline(sketch, "E248", {"points": [v(-57.56, -30.77) * mm, v(-57.48, -28.95) * mm, v(-57.4, -27.1) * mm, v(-57.33, -25.24) * mm]});
            skFitSpline(sketch, "E249", {"points": [v(-57.33, -25.24) * mm, v(-56.78, -25.16) * mm, v(-56.16, -25.1) * mm, v(-55.46, -25.07) * mm]});
            skFitSpline(sketch, "E250", {"points": [v(-55.46, -25.07) * mm, v(-54.76, -24.99) * mm, v(-53.9, -24.95) * mm, v(-52.9, -24.95) * mm]});
            skFitSpline(sketch, "E251", {"points": [v(-52.9, -24.95) * mm, v(-51.77, -24.95) * mm, v(-50.65, -25.05) * mm, v(-49.52, -25.24) * mm]});
            skFitSpline(sketch, "E252", {"points": [v(-49.52, -25.24) * mm, v(-48.4, -25.4) * mm, v(-47.39, -25.74) * mm, v(-46.5, -26.29) * mm]});
            skFitSpline(sketch, "E253", {"points": [v(-46.5, -26.29) * mm, v(-45.6, -26.8) * mm, v(-44.87, -27.53) * mm, v(-44.28, -28.5) * mm]});
            skFitSpline(sketch, "E254", {"points": [v(-44.28, -28.5) * mm, v(-43.7, -29.43) * mm, v(-43.4, -30.7) * mm, v(-43.4, -32.29) * mm]});
            skFitSpline(sketch, "E255", {"points": [v(-43.4, -32.29) * mm, v(-43.4, -33.92) * mm, v(-43.74, -35.27) * mm, v(-44.4, -36.36) * mm]});
            skFitSpline(sketch, "E256", {"points": [v(-44.4, -36.36) * mm, v(-45.02, -37.4) * mm, v(-45.86, -38.26) * mm, v(-46.9, -38.92) * mm]});
            skFitSpline(sketch, "E257", {"points": [v(-46.9, -38.92) * mm, v(-47.95, -39.54) * mm, v(-49.15, -40) * mm, v(-50.51, -40.26) * mm]});
            skFitSpline(sketch, "E258", {"points": [v(-50.51, -40.26) * mm, v(-51.83, -40.53) * mm, v(-53.17, -40.67) * mm, v(-54.53, -40.67) * mm]});
            skLineSegment(sketch, "E259", {"start": v(-54.53, -40.67) * mm, "end": v(-57.67, -40.67) * mm});
            skLineSegment(sketch, "E260", {"start": v(-57.67, -40.67) * mm, "end": v(-57.67, -36.3) * mm});
            skLineSegment(sketch, "E261", {"start": v(-57.67, -36.3) * mm, "end": v(-54.53, -40.67) * mm});
            skFitSpline(sketch, "E262", {"points": [v(-62.45, -47.83) * mm, v(-62.45, -50.4) * mm, v(-62.5, -52.92) * mm, v(-62.62, -55.4) * mm]});
            skFitSpline(sketch, "E263", {"points": [v(-62.62, -55.4) * mm, v(-62.7, -57.85) * mm, v(-62.8, -60.31) * mm, v(-62.92, -62.8) * mm]});
            skFitSpline(sketch, "E264", {"points": [v(-62.92, -62.8) * mm, v(-61.98, -62.72) * mm, v(-61.05, -62.68) * mm, v(-60.12, -62.68) * mm]});
            skFitSpline(sketch, "E265", {"points": [v(-60.12, -62.68) * mm, v(-59.15, -62.68) * mm, v(-58.2, -62.68) * mm, v(-57.27, -62.68) * mm]});
            skFitSpline(sketch, "E266", {"points": [v(-57.27, -62.68) * mm, v(-56.34, -62.68) * mm, v(-55.4, -62.7) * mm, v(-54.47, -62.74) * mm]});
            skFitSpline(sketch, "E267", {"points": [v(-54.47, -62.74) * mm, v(-53.5, -62.78) * mm, v(-52.55, -62.8) * mm, v(-51.62, -62.8) * mm]});
            skFitSpline(sketch, "E268", {"points": [v(-51.62, -62.8) * mm, v(-49.91, -62.8) * mm, v(-48.2, -62.62) * mm, v(-46.5, -62.27) * mm]});
            skFitSpline(sketch, "E269", {"points": [v(-46.5, -62.27) * mm, v(-44.75, -61.88) * mm, v(-43.16, -61.24) * mm, v(-41.72, -60.35) * mm]});
            skFitSpline(sketch, "E270", {"points": [v(-41.72, -60.35) * mm, v(-40.29, -59.42) * mm, v(-39.12, -58.21) * mm, v(-38.23, -56.74) * mm]});
            skFitSpline(sketch, "E271", {"points": [v(-38.23, -56.74) * mm, v(-37.34, -55.26) * mm, v(-36.89, -53.44) * mm, v(-36.89, -51.27) * mm]});
            skFitSpline(sketch, "E272", {"points": [v(-36.89, -51.27) * mm, v(-36.89, -47.93) * mm, v(-37.9, -45.5) * mm, v(-39.92, -43.99) * mm]});
            skFitSpline(sketch, "E273", {"points": [v(-39.92, -43.99) * mm, v(-41.9, -42.47) * mm, v(-44.61, -41.64) * mm, v(-48.07, -41.48) * mm]});
            skLineSegment(sketch, "E274", {"start": v(-62.45, -37.82) * mm, "end": v(-62.45, -47.83) * mm});
            skLineSegment(sketch, "E275", {"start": v(-62.45, -47.83) * mm, "end": v(-62.45, -37.82) * mm});
            skFitSpline(sketch, "E276", {"points": [v(-48.07, -41.37) * mm, v(-45.16, -40.7) * mm, v(-42.8, -39.56) * mm, v(-41.02, -37.93) * mm]});
            skFitSpline(sketch, "E277", {"points": [v(-41.02, -37.93) * mm, v(-39.2, -36.3) * mm, v(-38.29, -34.05) * mm, v(-38.29, -31.18) * mm]});
            skFitSpline(sketch, "E278", {"points": [v(-38.29, -31.18) * mm, v(-38.29, -29.55) * mm, v(-38.62, -28.19) * mm, v(-39.28, -27.1) * mm]});
            skFitSpline(sketch, "E279", {"points": [v(-39.28, -27.1) * mm, v(-39.94, -26.02) * mm, v(-40.83, -25.16) * mm, v(-41.95, -24.54) * mm]});
            skFitSpline(sketch, "E280", {"points": [v(-41.95, -24.54) * mm, v(-43.08, -23.88) * mm, v(-44.38, -23.43) * mm, v(-45.86, -23.2) * mm]});
            skFitSpline(sketch, "E281", {"points": [v(-45.86, -23.2) * mm, v(-47.33, -22.93) * mm, v(-48.9, -22.8) * mm, v(-50.57, -22.8) * mm]});
            skFitSpline(sketch, "E282", {"points": [v(-50.57, -22.8) * mm, v(-51.58, -22.8) * mm, v(-52.6, -22.85) * mm, v(-53.66, -22.97) * mm]});
            skFitSpline(sketch, "E283", {"points": [v(-53.66, -22.97) * mm, v(-54.7, -23.05) * mm, v(-55.73, -23.09) * mm, v(-56.74, -23.09) * mm]});
            skFitSpline(sketch, "E284", {"points": [v(-56.74, -23.09) * mm, v(-57.75, -23.09) * mm, v(-58.78, -23.07) * mm, v(-59.83, -23.03) * mm]});
            skFitSpline(sketch, "E285", {"points": [v(-59.83, -23.03) * mm, v(-60.88, -22.95) * mm, v(-61.9, -22.87) * mm, v(-62.92, -22.8) * mm]});
            skFitSpline(sketch, "E286", {"points": [v(-62.92, -22.8) * mm, v(-62.8, -25.28) * mm, v(-62.7, -27.76) * mm, v(-62.62, -30.25) * mm]});
            skFitSpline(sketch, "E287", {"points": [v(-62.62, -30.25) * mm, v(-62.5, -32.73) * mm, v(-62.45, -35.25) * mm, v(-62.45, -37.82) * mm]});
            skLineSegment(sketch, "E288", {"start": v(-48.07, -41.48) * mm, "end": v(-48.07, -41.37) * mm});
            skLineSegment(sketch, "E289", {"start": v(-48.07, -41.37) * mm, "end": v(-48.07, -41.48) * mm});
            skFitSpline(sketch, "E290", {"points": [v(-13.4, -57.03) * mm, v(-14.07, -58.12) * mm, v(-15.02, -59.07) * mm, v(-16.26, -59.88) * mm]});
            skFitSpline(sketch, "E291", {"points": [v(-16.26, -59.88) * mm, v(-17.46, -60.7) * mm, v(-18.8, -61.1) * mm, v(-20.28, -61.1) * mm]});
            skFitSpline(sketch, "E292", {"points": [v(-20.28, -61.1) * mm, v(-21.56, -61.1) * mm, v(-22.72, -60.64) * mm, v(-23.77, -59.7) * mm]});
            skFitSpline(sketch, "E293", {"points": [v(-23.77, -59.7) * mm, v(-24.82, -58.78) * mm, v(-25.34, -57.4) * mm, v(-25.34, -55.57) * mm]});
            skFitSpline(sketch, "E294", {"points": [v(-25.34, -55.57) * mm, v(-25.34, -54.49) * mm, v(-25.15, -53.6) * mm, v(-24.76, -52.9) * mm]});
            skFitSpline(sketch, "E295", {"points": [v(-24.76, -52.9) * mm, v(-24.33, -52.2) * mm, v(-23.79, -51.62) * mm, v(-23.13, -51.15) * mm]});
            skFitSpline(sketch, "E296", {"points": [v(-23.13, -51.15) * mm, v(-22.43, -50.68) * mm, v(-21.65, -50.32) * mm, v(-20.8, -50.04) * mm]});
            skFitSpline(sketch, "E297", {"points": [v(-20.8, -50.04) * mm, v(-19.9, -49.77) * mm, v(-19.01, -49.56) * mm, v(-18.12, -49.4) * mm]});
            skFitSpline(sketch, "E298", {"points": [v(-18.12, -49.4) * mm, v(-17.23, -49.2) * mm, v(-16.36, -49.03) * mm, v(-15.5, -48.88) * mm]});
            skFitSpline(sketch, "E299", {"points": [v(-15.5, -48.88) * mm, v(-14.6, -48.72) * mm, v(-13.83, -48.53) * mm, v(-13.17, -48.3) * mm]});
            skLineSegment(sketch, "E300", {"start": v(-13.17, -48.3) * mm, "end": v(-13.4, -57.03) * mm});
            skLineSegment(sketch, "E301", {"start": v(-13.4, -57.03) * mm, "end": v(-13.17, -48.3) * mm});
            skFitSpline(sketch, "E302", {"points": [v(-26.91, -40.96) * mm, v(-26.25, -39.72) * mm, v(-25.26, -38.75) * mm, v(-23.94, -38.05) * mm]});
            skFitSpline(sketch, "E303", {"points": [v(-23.94, -38.05) * mm, v(-22.59, -37.35) * mm, v(-21.13, -37) * mm, v(-19.58, -37) * mm]});
            skFitSpline(sketch, "E304", {"points": [v(-19.58, -37) * mm, v(-18.41, -37) * mm, v(-17.42, -37.21) * mm, v(-16.6, -37.64) * mm]});
            skFitSpline(sketch, "E305", {"points": [v(-16.6, -37.64) * mm, v(-15.8, -38.03) * mm, v(-15.13, -38.55) * mm, v(-14.63, -39.21) * mm]});
            skFitSpline(sketch, "E306", {"points": [v(-14.63, -39.21) * mm, v(-14.12, -39.87) * mm, v(-13.75, -40.65) * mm, v(-13.52, -41.54) * mm]});
            skFitSpline(sketch, "E307", {"points": [v(-13.52, -41.54) * mm, v(-13.29, -42.44) * mm, v(-13.17, -43.37) * mm, v(-13.17, -44.34) * mm]});
            skFitSpline(sketch, "E308", {"points": [v(-13.17, -44.34) * mm, v(-13.17, -44.92) * mm, v(-13.23, -45.4) * mm, v(-13.35, -45.8) * mm]});
            skFitSpline(sketch, "E309", {"points": [v(-13.35, -45.8) * mm, v(-13.46, -46.14) * mm, v(-13.81, -46.45) * mm, v(-14.4, -46.72) * mm]});
            skFitSpline(sketch, "E310", {"points": [v(-14.4, -46.72) * mm, v(-14.94, -47) * mm, v(-15.81, -47.27) * mm, v(-17.02, -47.54) * mm]});
            skFitSpline(sketch, "E311", {"points": [v(-17.02, -47.54) * mm, v(-18.18, -47.77) * mm, v(-19.81, -48.06) * mm, v(-21.9, -48.41) * mm]});
            skFitSpline(sketch, "E312", {"points": [v(-21.9, -48.41) * mm, v(-24.47, -48.84) * mm, v(-26.49, -49.7) * mm, v(-27.96, -50.97) * mm]});
            skFitSpline(sketch, "E313", {"points": [v(-27.96, -50.97) * mm, v(-29.4, -52.26) * mm, v(-30.12, -54.06) * mm, v(-30.12, -56.39) * mm]});
            skFitSpline(sketch, "E314", {"points": [v(-30.12, -56.39) * mm, v(-30.12, -57.52) * mm, v(-29.9, -58.52) * mm, v(-29.48, -59.42) * mm]});
            skFitSpline(sketch, "E315", {"points": [v(-29.48, -59.42) * mm, v(-29, -60.27) * mm, v(-28.43, -61) * mm, v(-27.73, -61.63) * mm]});
            skFitSpline(sketch, "E316", {"points": [v(-27.73, -61.63) * mm, v(-27, -62.25) * mm, v(-26.16, -62.7) * mm, v(-25.22, -62.97) * mm]});
            skFitSpline(sketch, "E317", {"points": [v(-25.22, -62.97) * mm, v(-24.3, -63.24) * mm, v(-23.34, -63.38) * mm, v(-22.37, -63.38) * mm]});
            skFitSpline(sketch, "E318", {"points": [v(-22.37, -63.38) * mm, v(-20.4, -63.38) * mm, v(-18.72, -63.05) * mm, v(-17.36, -62.39) * mm]});
            skFitSpline(sketch, "E319", {"points": [v(-17.36, -62.39) * mm, v(-16, -61.73) * mm, v(-14.63, -60.7) * mm, v(-13.23, -59.3) * mm]});
            skFitSpline(sketch, "E320", {"points": [v(-13.23, -59.3) * mm, v(-13.11, -60.31) * mm, v(-12.73, -61.14) * mm, v(-12.07, -61.8) * mm]});
            skFitSpline(sketch, "E321", {"points": [v(-12.07, -61.8) * mm, v(-11.4, -62.43) * mm, v(-10.46, -62.74) * mm, v(-9.21, -62.74) * mm]});
            skFitSpline(sketch, "E322", {"points": [v(-9.21, -62.74) * mm, v(-8.44, -62.74) * mm, v(-7.74, -62.68) * mm, v(-7.12, -62.56) * mm]});
            skFitSpline(sketch, "E323", {"points": [v(-7.12, -62.56) * mm, v(-6.46, -62.45) * mm, v(-5.91, -62.29) * mm, v(-5.49, -62.1) * mm]});
            skLineSegment(sketch, "E324", {"start": v(-27.55, -37.93) * mm, "end": v(-27.55, -40.96) * mm});
            skLineSegment(sketch, "E325", {"start": v(-27.55, -40.96) * mm, "end": v(-26.91, -40.96) * mm});
            skLineSegment(sketch, "E326", {"start": v(-26.91, -40.96) * mm, "end": v(-27.55, -37.93) * mm});
            skFitSpline(sketch, "E327", {"points": [v(-5.49, -60.81) * mm, v(-5.68, -60.93) * mm, v(-5.9, -61) * mm, v(-6.13, -61.05) * mm]});
            skFitSpline(sketch, "E328", {"points": [v(-6.13, -61.05) * mm, v(-6.32, -61.05) * mm, v(-6.52, -61.05) * mm, v(-6.7, -61.05) * mm]});
            skFitSpline(sketch, "E329", {"points": [v(-6.7, -61.05) * mm, v(-7.3, -61.05) * mm, v(-7.74, -60.91) * mm, v(-8.05, -60.64) * mm]});
            skFitSpline(sketch, "E330", {"points": [v(-8.05, -60.64) * mm, v(-8.32, -60.37) * mm, v(-8.53, -60.04) * mm, v(-8.69, -59.65) * mm]});
            skFitSpline(sketch, "E331", {"points": [v(-8.69, -59.65) * mm, v(-8.84, -59.22) * mm, v(-8.94, -58.76) * mm, v(-8.98, -58.25) * mm]});
            skFitSpline(sketch, "E332", {"points": [v(-8.98, -58.25) * mm, v(-8.98, -57.7) * mm, v(-8.98, -57.2) * mm, v(-8.98, -56.74) * mm]});
            skFitSpline(sketch, "E333", {"points": [v(-8.98, -56.74) * mm, v(-8.98, -54.3) * mm, v(-8.94, -51.98) * mm, v(-8.86, -49.81) * mm]});
            skFitSpline(sketch, "E334", {"points": [v(-8.86, -49.81) * mm, v(-8.79, -47.6) * mm, v(-8.75, -45.39) * mm, v(-8.75, -43.17) * mm]});
            skFitSpline(sketch, "E335", {"points": [v(-8.75, -43.17) * mm, v(-8.75, -41.9) * mm, v(-8.98, -40.73) * mm, v(-9.45, -39.68) * mm]});
            skFitSpline(sketch, "E336", {"points": [v(-9.45, -39.68) * mm, v(-9.91, -38.6) * mm, v(-10.55, -37.68) * mm, v(-11.37, -36.94) * mm]});
            skFitSpline(sketch, "E337", {"points": [v(-11.37, -36.94) * mm, v(-12.18, -36.17) * mm, v(-13.17, -35.58) * mm, v(-14.34, -35.2) * mm]});
            skFitSpline(sketch, "E338", {"points": [v(-14.34, -35.2) * mm, v(-15.5, -34.77) * mm, v(-16.78, -34.56) * mm, v(-18.18, -34.56) * mm]});
            skFitSpline(sketch, "E339", {"points": [v(-18.18, -34.56) * mm, v(-19.73, -34.56) * mm, v(-21.25, -34.79) * mm, v(-22.72, -35.25) * mm]});
            skFitSpline(sketch, "E340", {"points": [v(-22.72, -35.25) * mm, v(-24.2, -35.72) * mm, v(-25.8, -36.61) * mm, v(-27.55, -37.93) * mm]});
            skLineSegment(sketch, "E341", {"start": v(-5.49, -62.1) * mm, "end": v(-5.49, -60.81) * mm});
            skLineSegment(sketch, "E342", {"start": v(-5.49, -60.81) * mm, "end": v(-5.49, -62.1) * mm});
            skFitSpline(sketch, "E343", {"points": [v(-0.13, -57.38) * mm, v(-0.13, -57.96) * mm, v(-0.26, -58.7) * mm, v(-0.54, -59.6) * mm]});
            skFitSpline(sketch, "E344", {"points": [v(-0.54, -59.6) * mm, v(-0.77, -60.45) * mm, v(-1, -61.13) * mm, v(-1.23, -61.63) * mm]});
            skFitSpline(sketch, "E345", {"points": [v(-1.23, -61.63) * mm, v(-0.42, -62.1) * mm, v(0.6, -62.5) * mm, v(1.8, -62.85) * mm]});
            skFitSpline(sketch, "E346", {"points": [v(1.8, -62.85) * mm, v(3, -63.2) * mm, v(4.5, -63.38) * mm, v(6.28, -63.38) * mm]});
            skFitSpline(sketch, "E347", {"points": [v(6.28, -63.38) * mm, v(7.9, -63.38) * mm, v(9.36, -63.14) * mm, v(10.64, -62.68) * mm]});
            skFitSpline(sketch, "E348", {"points": [v(10.64, -62.68) * mm, v(11.92, -62.17) * mm, v(13.01, -61.5) * mm, v(13.9, -60.64) * mm]});
            skFitSpline(sketch, "E349", {"points": [v(13.9, -60.64) * mm, v(14.84, -59.75) * mm, v(15.53, -58.76) * mm, v(16, -57.67) * mm]});
            skFitSpline(sketch, "E350", {"points": [v(16, -57.67) * mm, v(16.5, -56.58) * mm, v(16.76, -55.48) * mm, v(16.76, -54.35) * mm]});
            skFitSpline(sketch, "E351", {"points": [v(16.76, -54.35) * mm, v(16.76, -52.72) * mm, v(16.4, -51.44) * mm, v(15.7, -50.5) * mm]});
            skFitSpline(sketch, "E352", {"points": [v(15.7, -50.5) * mm, v(15.05, -49.58) * mm, v(14.21, -48.86) * mm, v(13.2, -48.35) * mm]});
            skFitSpline(sketch, "E353", {"points": [v(13.2, -48.35) * mm, v(12.2, -47.81) * mm, v(11.1, -47.4) * mm, v(9.89, -47.13) * mm]});
            skFitSpline(sketch, "E354", {"points": [v(9.89, -47.13) * mm, v(8.68, -46.82) * mm, v(7.58, -46.47) * mm, v(6.57, -46.08) * mm]});
            skFitSpline(sketch, "E355", {"points": [v(6.57, -46.08) * mm, v(5.56, -45.7) * mm, v(4.7, -45.17) * mm, v(4, -44.51) * mm]});
            skFitSpline(sketch, "E356", {"points": [v(4, -44.51) * mm, v(3.35, -43.81) * mm, v(3.02, -42.84) * mm, v(3.02, -41.6) * mm]});
            skFitSpline(sketch, "E357", {"points": [v(3.02, -41.6) * mm, v(3.02, -40.75) * mm, v(3.17, -40) * mm, v(3.48, -39.39) * mm]});
            skFitSpline(sketch, "E358", {"points": [v(3.48, -39.39) * mm, v(3.8, -38.77) * mm, v(4.18, -38.26) * mm, v(4.65, -37.87) * mm]});
            skFitSpline(sketch, "E359", {"points": [v(4.65, -37.87) * mm, v(5.11, -37.49) * mm, v(5.64, -37.2) * mm, v(6.22, -37) * mm]});
            skFitSpline(sketch, "E360", {"points": [v(6.22, -37) * mm, v(6.8, -36.8) * mm, v(7.38, -36.71) * mm, v(7.97, -36.71) * mm]});
            skFitSpline(sketch, "E361", {"points": [v(7.97, -36.71) * mm, v(9.29, -36.71) * mm, v(10.4, -37.08) * mm, v(11.28, -37.82) * mm]});
            skFitSpline(sketch, "E362", {"points": [v(11.28, -37.82) * mm, v(12.18, -38.55) * mm, v(12.78, -39.39) * mm, v(13.09, -40.32) * mm]});
            skLineSegment(sketch, "E363", {"start": v(0.57, -57.38) * mm, "end": v(-0.13, -57.38) * mm});
            skLineSegment(sketch, "E364", {"start": v(-0.13, -57.38) * mm, "end": v(0.57, -57.38) * mm});
            skFitSpline(sketch, "E365", {"points": [v(13.79, -40.32) * mm, v(13.87, -39.85) * mm, v(14.04, -39.2) * mm, v(14.31, -38.34) * mm]});
            skFitSpline(sketch, "E366", {"points": [v(14.31, -38.34) * mm, v(14.58, -37.49) * mm, v(14.87, -36.77) * mm, v(15.19, -36.19) * mm]});
            skFitSpline(sketch, "E367", {"points": [v(15.19, -36.19) * mm, v(14.3, -35.88) * mm, v(13.34, -35.53) * mm, v(12.33, -35.14) * mm]});
            skFitSpline(sketch, "E368", {"points": [v(12.33, -35.14) * mm, v(11.36, -34.75) * mm, v(10.16, -34.56) * mm, v(8.72, -34.56) * mm]});
            skFitSpline(sketch, "E369", {"points": [v(8.72, -34.56) * mm, v(7.17, -34.56) * mm, v(5.8, -34.79) * mm, v(4.59, -35.25) * mm]});
            skFitSpline(sketch, "E370", {"points": [v(4.59, -35.25) * mm, v(3.39, -35.68) * mm, v(2.38, -36.28) * mm, v(1.56, -37.06) * mm]});
            skFitSpline(sketch, "E371", {"points": [v(1.56, -37.06) * mm, v(0.75, -37.84) * mm, v(0.12, -38.77) * mm, v(-0.3, -39.85) * mm]});
            skFitSpline(sketch, "E372", {"points": [v(-0.3, -39.85) * mm, v(-0.73, -40.9) * mm, v(-0.94, -42.07) * mm, v(-0.94, -43.35) * mm]});
            skFitSpline(sketch, "E373", {"points": [v(-0.94, -43.35) * mm, v(-0.94, -44.98) * mm, v(-0.61, -46.26) * mm, v(0.05, -47.2) * mm]});
            skFitSpline(sketch, "E374", {"points": [v(0.05, -47.2) * mm, v(0.75, -48.12) * mm, v(1.6, -48.88) * mm, v(2.6, -49.46) * mm]});
            skFitSpline(sketch, "E375", {"points": [v(2.6, -49.46) * mm, v(3.62, -50) * mm, v(4.72, -50.43) * mm, v(5.93, -50.74) * mm]});
            skFitSpline(sketch, "E376", {"points": [v(5.93, -50.74) * mm, v(7.13, -51.05) * mm, v(8.24, -51.42) * mm, v(9.25, -51.85) * mm]});
            skFitSpline(sketch, "E377", {"points": [v(9.25, -51.85) * mm, v(10.26, -52.24) * mm, v(11.1, -52.76) * mm, v(11.75, -53.42) * mm]});
            skFitSpline(sketch, "E378", {"points": [v(11.75, -53.42) * mm, v(12.45, -54.04) * mm, v(12.8, -54.95) * mm, v(12.8, -56.16) * mm]});
            skFitSpline(sketch, "E379", {"points": [v(12.8, -56.16) * mm, v(12.8, -57.01) * mm, v(12.64, -57.77) * mm, v(12.33, -58.43) * mm]});
            skFitSpline(sketch, "E380", {"points": [v(12.33, -58.43) * mm, v(12.02, -59.09) * mm, v(11.6, -59.63) * mm, v(11.05, -60.06) * mm]});
            skFitSpline(sketch, "E381", {"points": [v(11.05, -60.06) * mm, v(10.55, -60.48) * mm, v(9.95, -60.81) * mm, v(9.25, -61.05) * mm]});
            skFitSpline(sketch, "E382", {"points": [v(9.25, -61.05) * mm, v(8.59, -61.28) * mm, v(7.89, -61.4) * mm, v(7.15, -61.4) * mm]});
            skFitSpline(sketch, "E383", {"points": [v(7.15, -61.4) * mm, v(6.34, -61.4) * mm, v(5.56, -61.26) * mm, v(4.82, -60.99) * mm]});
            skFitSpline(sketch, "E384", {"points": [v(4.82, -60.99) * mm, v(4.12, -60.72) * mm, v(3.48, -60.39) * mm, v(2.9, -60) * mm]});
            skFitSpline(sketch, "E385", {"points": [v(2.9, -60) * mm, v(2.36, -59.57) * mm, v(1.87, -59.13) * mm, v(1.44, -58.66) * mm]});
            skFitSpline(sketch, "E386", {"points": [v(1.44, -58.66) * mm, v(1.06, -58.2) * mm, v(0.77, -57.77) * mm, v(0.57, -57.38) * mm]});
            skLineSegment(sketch, "E387", {"start": v(13.09, -40.32) * mm, "end": v(13.79, -40.32) * mm});
            skLineSegment(sketch, "E388", {"start": v(13.79, -40.32) * mm, "end": v(13.09, -40.32) * mm});
            skFitSpline(sketch, "E389", {"points": [v(23.67, -29.37) * mm, v(23.74, -30.62) * mm, v(23.78, -31.82) * mm, v(23.78, -32.98) * mm]});
            skFitSpline(sketch, "E390", {"points": [v(23.78, -32.98) * mm, v(23.82, -34.15) * mm, v(23.86, -35.12) * mm, v(23.9, -35.9) * mm]});
            skFitSpline(sketch, "E391", {"points": [v(23.9, -35.9) * mm, v(23.08, -35.9) * mm, v(21.8, -35.84) * mm, v(20.06, -35.72) * mm]});
            skFitSpline(sketch, "E392", {"points": [v(20.06, -35.72) * mm, v(20.1, -35.91) * mm, v(20.12, -36.1) * mm, v(20.12, -36.3) * mm]});
            skFitSpline(sketch, "E393", {"points": [v(20.12, -36.3) * mm, v(20.15, -36.5) * mm, v(20.17, -36.7) * mm, v(20.17, -36.88) * mm]});
            skFitSpline(sketch, "E394", {"points": [v(20.17, -36.88) * mm, v(20.17, -37.12) * mm, v(20.15, -37.35) * mm, v(20.12, -37.58) * mm]});
            skFitSpline(sketch, "E395", {"points": [v(20.12, -37.58) * mm, v(20.12, -37.78) * mm, v(20.1, -38) * mm, v(20.06, -38.22) * mm]});
            skFitSpline(sketch, "E396", {"points": [v(20.06, -38.22) * mm, v(20.45, -38.19) * mm, v(20.81, -38.17) * mm, v(21.16, -38.17) * mm]});
            skFitSpline(sketch, "E397", {"points": [v(21.16, -38.17) * mm, v(21.51, -38.13) * mm, v(21.84, -38.1) * mm, v(22.15, -38.1) * mm]});
            skLineSegment(sketch, "E398", {"start": v(28.5, -27.34) * mm, "end": v(23.67, -29.37) * mm});
            skLineSegment(sketch, "E399", {"start": v(23.67, -29.37) * mm, "end": v(28.5, -27.34) * mm});
            skFitSpline(sketch, "E400", {"points": [v(24.02, -38.1) * mm, v(24.02, -40.28) * mm, v(24, -42.26) * mm, v(23.96, -44.05) * mm]});
            skFitSpline(sketch, "E401", {"points": [v(23.96, -44.05) * mm, v(23.92, -45.8) * mm, v(23.86, -47.4) * mm, v(23.78, -48.88) * mm]});
            skFitSpline(sketch, "E402", {"points": [v(23.78, -48.88) * mm, v(23.74, -50.32) * mm, v(23.7, -51.65) * mm, v(23.67, -52.9) * mm]});
            skFitSpline(sketch, "E403", {"points": [v(23.67, -52.9) * mm, v(23.63, -54.1) * mm, v(23.6, -55.23) * mm, v(23.6, -56.27) * mm]});
            skFitSpline(sketch, "E404", {"points": [v(23.6, -56.27) * mm, v(23.6, -58.6) * mm, v(24.2, -60.37) * mm, v(25.36, -61.57) * mm]});
            skFitSpline(sketch, "E405", {"points": [v(25.36, -61.57) * mm, v(26.52, -62.78) * mm, v(28.32, -63.38) * mm, v(30.77, -63.38) * mm]});
            skFitSpline(sketch, "E406", {"points": [v(30.77, -63.38) * mm, v(31.5, -63.38) * mm, v(32.26, -63.28) * mm, v(33.04, -63.09) * mm]});
            skFitSpline(sketch, "E407", {"points": [v(33.04, -63.09) * mm, v(33.86, -62.93) * mm, v(34.6, -62.8) * mm, v(35.25, -62.68) * mm]});
            skLineSegment(sketch, "E408", {"start": v(22.15, -38.1) * mm, "end": v(24.02, -38.1) * mm});
            skLineSegment(sketch, "E409", {"start": v(24.02, -38.1) * mm, "end": v(22.15, -38.1) * mm});
            skFitSpline(sketch, "E410", {"points": [v(35.25, -61.28) * mm, v(34.87, -61.4) * mm, v(34.4, -61.5) * mm, v(33.86, -61.57) * mm]});
            skFitSpline(sketch, "E411", {"points": [v(33.86, -61.57) * mm, v(33.35, -61.65) * mm, v(32.94, -61.69) * mm, v(32.63, -61.69) * mm]});
            skFitSpline(sketch, "E412", {"points": [v(32.63, -61.69) * mm, v(31.47, -61.69) * mm, v(30.58, -61.44) * mm, v(29.96, -60.93) * mm]});
            skFitSpline(sketch, "E413", {"points": [v(29.96, -60.93) * mm, v(29.33, -60.43) * mm, v(28.87, -59.77) * mm, v(28.56, -58.95) * mm]});
            skFitSpline(sketch, "E414", {"points": [v(28.56, -58.95) * mm, v(28.25, -58.1) * mm, v(28.05, -57.15) * mm, v(27.98, -56.1) * mm]});
            skFitSpline(sketch, "E415", {"points": [v(27.98, -56.1) * mm, v(27.94, -55.05) * mm, v(27.92, -53.98) * mm, v(27.92, -52.9) * mm]});
            skFitSpline(sketch, "E416", {"points": [v(27.92, -52.9) * mm, v(27.92, -51.62) * mm, v(27.92, -50.16) * mm, v(27.92, -48.53) * mm]});
            skFitSpline(sketch, "E417", {"points": [v(27.92, -48.53) * mm, v(27.96, -46.9) * mm, v(28, -45.35) * mm, v(28.03, -43.87) * mm]});
            skFitSpline(sketch, "E418", {"points": [v(28.03, -43.87) * mm, v(28.07, -42.36) * mm, v(28.11, -41.06) * mm, v(28.15, -39.97) * mm]});
            skFitSpline(sketch, "E419", {"points": [v(28.15, -39.97) * mm, v(28.23, -38.88) * mm, v(28.29, -38.26) * mm, v(28.32, -38.1) * mm]});
            skLineSegment(sketch, "E420", {"start": v(35.25, -62.68) * mm, "end": v(35.25, -61.28) * mm});
            skLineSegment(sketch, "E421", {"start": v(35.25, -61.28) * mm, "end": v(35.25, -62.68) * mm});
            skFitSpline(sketch, "E422", {"points": [v(31.18, -38.1) * mm, v(31.8, -38.1) * mm, v(32.38, -38.13) * mm, v(32.92, -38.17) * mm]});
            skFitSpline(sketch, "E423", {"points": [v(32.92, -38.17) * mm, v(33.47, -38.17) * mm, v(34, -38.19) * mm, v(34.5, -38.22) * mm]});
            skFitSpline(sketch, "E424", {"points": [v(34.5, -38.22) * mm, v(34.46, -38.1) * mm, v(34.44, -37.91) * mm, v(34.44, -37.64) * mm]});
            skLineSegment(sketch, "E425", {"start": v(28.32, -38.1) * mm, "end": v(31.18, -38.1) * mm});
            skLineSegment(sketch, "E426", {"start": v(31.18, -38.1) * mm, "end": v(28.32, -38.1) * mm});
            skFitSpline(sketch, "E427", {"points": [v(34.44, -36.42) * mm, v(34.44, -36.1) * mm, v(34.46, -35.9) * mm, v(34.5, -35.78) * mm]});
            skFitSpline(sketch, "E428", {"points": [v(34.5, -35.78) * mm, v(33.14, -35.86) * mm, v(31.88, -35.91) * mm, v(30.71, -35.95) * mm]});
            skFitSpline(sketch, "E429", {"points": [v(30.71, -35.95) * mm, v(29.55, -35.95) * mm, v(28.75, -35.95) * mm, v(28.32, -35.95) * mm]});
            skFitSpline(sketch, "E430", {"points": [v(28.32, -35.95) * mm, v(28.4, -34.52) * mm, v(28.46, -33.1) * mm, v(28.5, -31.7) * mm]});
            skFitSpline(sketch, "E431", {"points": [v(28.5, -31.7) * mm, v(28.58, -30.27) * mm, v(28.67, -28.81) * mm, v(28.8, -27.34) * mm]});
            skLineSegment(sketch, "E432", {"start": v(34.44, -37.64) * mm, "end": v(34.44, -37) * mm});
            skLineSegment(sketch, "E433", {"start": v(34.44, -37) * mm, "end": v(34.44, -36.42) * mm});
            skLineSegment(sketch, "E434", {"start": v(34.44, -36.42) * mm, "end": v(34.44, -37.64) * mm});
            skFitSpline(sketch, "E435", {"points": [v(39.75, -54) * mm, v(39.75, -57.03) * mm, v(40.6, -59.36) * mm, v(42.32, -60.99) * mm]});
            skFitSpline(sketch, "E436", {"points": [v(42.32, -60.99) * mm, v(44.06, -62.58) * mm, v(46.45, -63.38) * mm, v(49.48, -63.38) * mm]});
            skFitSpline(sketch, "E437", {"points": [v(49.48, -63.38) * mm, v(51.34, -63.38) * mm, v(53.07, -62.95) * mm, v(54.66, -62.1) * mm]});
            skFitSpline(sketch, "E438", {"points": [v(54.66, -62.1) * mm, v(56.25, -61.2) * mm, v(57.55, -59.83) * mm, v(58.56, -57.96) * mm]});
            skLineSegment(sketch, "E439", {"start": v(28.8, -27.34) * mm, "end": v(28.5, -27.34) * mm});
            skLineSegment(sketch, "E440", {"start": v(28.5, -27.34) * mm, "end": v(28.8, -27.34) * mm});
            skFitSpline(sketch, "E441", {"points": [v(58.68, -60.47) * mm, v(58.68, -60.9) * mm, v(58.66, -61.3) * mm, v(58.62, -61.69) * mm]});
            skFitSpline(sketch, "E442", {"points": [v(58.62, -61.69) * mm, v(58.62, -62.08) * mm, v(58.6, -62.45) * mm, v(58.56, -62.8) * mm]});
            skFitSpline(sketch, "E443", {"points": [v(58.56, -62.8) * mm, v(59.34, -62.72) * mm, v(60.1, -62.68) * mm, v(60.83, -62.68) * mm]});
            skFitSpline(sketch, "E444", {"points": [v(60.83, -62.68) * mm, v(61.57, -62.68) * mm, v(62.33, -62.72) * mm, v(63.1, -62.8) * mm]});
            skFitSpline(sketch, "E445", {"points": [v(63.1, -62.8) * mm, v(63.02, -61.24) * mm, v(62.97, -59.63) * mm, v(62.93, -57.96) * mm]});
            skFitSpline(sketch, "E446", {"points": [v(62.93, -57.96) * mm, v(62.89, -56.3) * mm, v(62.87, -54.58) * mm, v(62.87, -52.84) * mm]});
            skFitSpline(sketch, "E447", {"points": [v(62.87, -52.84) * mm, v(62.87, -49.7) * mm, v(62.89, -46.72) * mm, v(62.93, -43.93) * mm]});
            skFitSpline(sketch, "E448", {"points": [v(62.93, -43.93) * mm, v(62.97, -41.1) * mm, v(63.08, -38.17) * mm, v(63.28, -35.14) * mm]});
            skFitSpline(sketch, "E449", {"points": [v(63.28, -35.14) * mm, v(62.89, -35.22) * mm, v(62.5, -35.3) * mm, v(62.11, -35.37) * mm]});
            skFitSpline(sketch, "E450", {"points": [v(62.11, -35.37) * mm, v(61.72, -35.4) * mm, v(61.32, -35.43) * mm, v(60.89, -35.43) * mm]});
            skFitSpline(sketch, "E451", {"points": [v(60.89, -35.43) * mm, v(60.46, -35.43) * mm, v(60.05, -35.4) * mm, v(59.67, -35.37) * mm]});
            skFitSpline(sketch, "E452", {"points": [v(59.67, -35.37) * mm, v(59.28, -35.3) * mm, v(58.87, -35.22) * mm, v(58.44, -35.14) * mm]});
            skFitSpline(sketch, "E453", {"points": [v(58.44, -35.14) * mm, v(58.48, -35.84) * mm, v(58.5, -36.57) * mm, v(58.5, -37.35) * mm]});
            skFitSpline(sketch, "E454", {"points": [v(58.5, -37.35) * mm, v(58.54, -38.13) * mm, v(58.56, -38.94) * mm, v(58.56, -39.8) * mm]});
            skLineSegment(sketch, "E455", {"start": v(58.56, -57.96) * mm, "end": v(58.68, -57.96) * mm});
            skLineSegment(sketch, "E456", {"start": v(58.68, -57.96) * mm, "end": v(58.68, -60.47) * mm});
            skLineSegment(sketch, "E457", {"start": v(58.68, -60.47) * mm, "end": v(58.56, -57.96) * mm});
            skFitSpline(sketch, "E458", {"points": [v(58.56, -44.69) * mm, v(58.56, -46.98) * mm, v(58.54, -48.78) * mm, v(58.5, -50.1) * mm]});
            skFitSpline(sketch, "E459", {"points": [v(58.5, -50.1) * mm, v(58.5, -51.42) * mm, v(58.44, -52.47) * mm, v(58.33, -53.25) * mm]});
            skFitSpline(sketch, "E460", {"points": [v(58.33, -53.25) * mm, v(58.25, -54.02) * mm, v(58.13, -54.64) * mm, v(57.98, -55.1) * mm]});
            skFitSpline(sketch, "E461", {"points": [v(57.98, -55.1) * mm, v(57.82, -55.57) * mm, v(57.6, -56.14) * mm, v(57.34, -56.8) * mm]});
            skFitSpline(sketch, "E462", {"points": [v(57.34, -56.8) * mm, v(56.83, -57.85) * mm, v(56.04, -58.74) * mm, v(54.95, -59.48) * mm]});
            skFitSpline(sketch, "E463", {"points": [v(54.95, -59.48) * mm, v(53.86, -60.17) * mm, v(52.5, -60.52) * mm, v(50.87, -60.52) * mm]});
            skFitSpline(sketch, "E464", {"points": [v(50.87, -60.52) * mm, v(49.75, -60.52) * mm, v(48.76, -60.33) * mm, v(47.9, -59.94) * mm]});
            skFitSpline(sketch, "E465", {"points": [v(47.9, -59.94) * mm, v(47.1, -59.51) * mm, v(46.41, -59) * mm, v(45.87, -58.37) * mm]});
            skFitSpline(sketch, "E466", {"points": [v(45.87, -58.37) * mm, v(45.36, -57.83) * mm, v(44.94, -57.03) * mm, v(44.59, -55.98) * mm]});
            skFitSpline(sketch, "E467", {"points": [v(44.59, -55.98) * mm, v(44.24, -54.9) * mm, v(44.06, -53.34) * mm, v(44.06, -51.32) * mm]});
            skFitSpline(sketch, "E468", {"points": [v(44.06, -51.32) * mm, v(44.06, -48.41) * mm, v(44.1, -45.58) * mm, v(44.18, -42.82) * mm]});
            skFitSpline(sketch, "E469", {"points": [v(44.18, -42.82) * mm, v(44.3, -40.03) * mm, v(44.45, -37.47) * mm, v(44.64, -35.14) * mm]});
            skFitSpline(sketch, "E470", {"points": [v(44.64, -35.14) * mm, v(43.67, -35.33) * mm, v(42.88, -35.43) * mm, v(42.26, -35.43) * mm]});
            skFitSpline(sketch, "E471", {"points": [v(42.26, -35.43) * mm, v(41.6, -35.43) * mm, v(40.78, -35.33) * mm, v(39.81, -35.14) * mm]});
            skFitSpline(sketch, "E472", {"points": [v(39.81, -35.14) * mm, v(39.85, -36.77) * mm, v(39.87, -38.38) * mm, v(39.87, -39.97) * mm]});
            skFitSpline(sketch, "E473", {"points": [v(39.87, -39.97) * mm, v(39.9, -41.56) * mm, v(39.93, -43.04) * mm, v(39.93, -44.4) * mm]});
            skFitSpline(sketch, "E474", {"points": [v(39.93, -44.4) * mm, v(39.93, -45.83) * mm, v(39.9, -47.29) * mm, v(39.81, -48.76) * mm]});
            skFitSpline(sketch, "E475", {"points": [v(39.81, -48.76) * mm, v(39.77, -50.2) * mm, v(39.75, -51.95) * mm, v(39.75, -54) * mm]});
            skLineSegment(sketch, "E476", {"start": v(58.56, -39.8) * mm, "end": v(58.56, -44.69) * mm});
            skLineSegment(sketch, "E477", {"start": v(58.56, -44.69) * mm, "end": v(58.56, -39.8) * mm});
            skSolve(sketch);
        }
        {
            var Q0;
            Q0=makeQuery(id+"F0.imprint","IMPRINT",FACE,{"disambiguationData":[TD([[makeQuery(id+"F0.imprint","IMPRINT",EDGE,{"derivedFrom":sQuery(id+"F0.wireOp",EDGE,"E0")}),1.0]])]});
            var Q1;
            Q1=makeQuery(id+"F0.imprint","IMPRINT",FACE,{"disambiguationData":[TD([[makeQuery(id+"F0.imprint","IMPRINT",EDGE,{"derivedFrom":sQuery(id+"F0.wireOp",EDGE,"E48")}),1.0]])]});
            var Q2;
            Q2=makeQuery(id+"F0.imprint","IMPRINT",FACE,{"disambiguationData":[TD([[makeQuery(id+"F0.imprint","IMPRINT",EDGE,{"derivedFrom":sQuery(id+"F0.wireOp",EDGE,"E75")}),1.0]])]});
            var Q3;
            Q3=makeQuery(id+"F0.imprint","IMPRINT",FACE,{"disambiguationData":[TD([[makeQuery(id+"F0.imprint","IMPRINT",EDGE,{"derivedFrom":sQuery(id+"F0.wireOp",EDGE,"E108")}),1.0]])]});
            var Q4;
            Q4=makeQuery(id+"F0.imprint","IMPRINT",FACE,{"disambiguationData":[TD([[makeQuery(id+"F0.imprint","IMPRINT",EDGE,{"derivedFrom":sQuery(id+"F0.wireOp",EDGE,"E161")}),1.0]])]});
            var Q5;
            Q5=makeQuery(id+"F0.imprint","IMPRINT",FACE,{"disambiguationData":[TD([[makeQuery(id+"F0.imprint","IMPRINT",EDGE,{"derivedFrom":sQuery(id+"F0.wireOp",EDGE,"E214")}),1.0]])]});
            var Q6;
            Q6=makeQuery(id+"F0.imprint","IMPRINT",FACE,{"disambiguationData":[TD([[makeQuery(id+"F0.imprint","IMPRINT",EDGE,{"derivedFrom":sQuery(id+"F0.wireOp",EDGE,"E232")}),1.0]])]});
            var Q7;
            Q7=makeQuery(id+"F0.imprint","IMPRINT",FACE,{"disambiguationData":[TD([[makeQuery(id+"F0.imprint","IMPRINT",EDGE,{"derivedFrom":sQuery(id+"F0.wireOp",EDGE,"E290")}),1.0]])]});
            var Q8;
            Q8=makeQuery(id+"F0.imprint","IMPRINT",FACE,{"disambiguationData":[TD([[makeQuery(id+"F0.imprint","IMPRINT",EDGE,{"derivedFrom":sQuery(id+"F0.wireOp",EDGE,"E343")}),1.0]])]});
            var Q9;
            Q9=makeQuery(id+"F0.imprint","IMPRINT",FACE,{"disambiguationData":[TD([[makeQuery(id+"F0.imprint","IMPRINT",EDGE,{"derivedFrom":sQuery(id+"F0.wireOp",EDGE,"E389")}),1.0]])]});
            var Q10;
            Q10=makeQuery(id+"F0.imprint","IMPRINT",FACE,{"disambiguationData":[TD([[makeQuery(id+"F0.imprint","IMPRINT",EDGE,{"derivedFrom":sQuery(id+"F0.wireOp",EDGE,"E435")}),1.0]])]});
            extrude(context, id + "F1", {"entities" : qUnion([Q0, Q1, Q2, Q3, Q4, Q5, Q6, Q7, Q8, Q9, Q10]), "depth" : 2 * mm, "offsetDistance" : 25 * mm});
        }
    });
